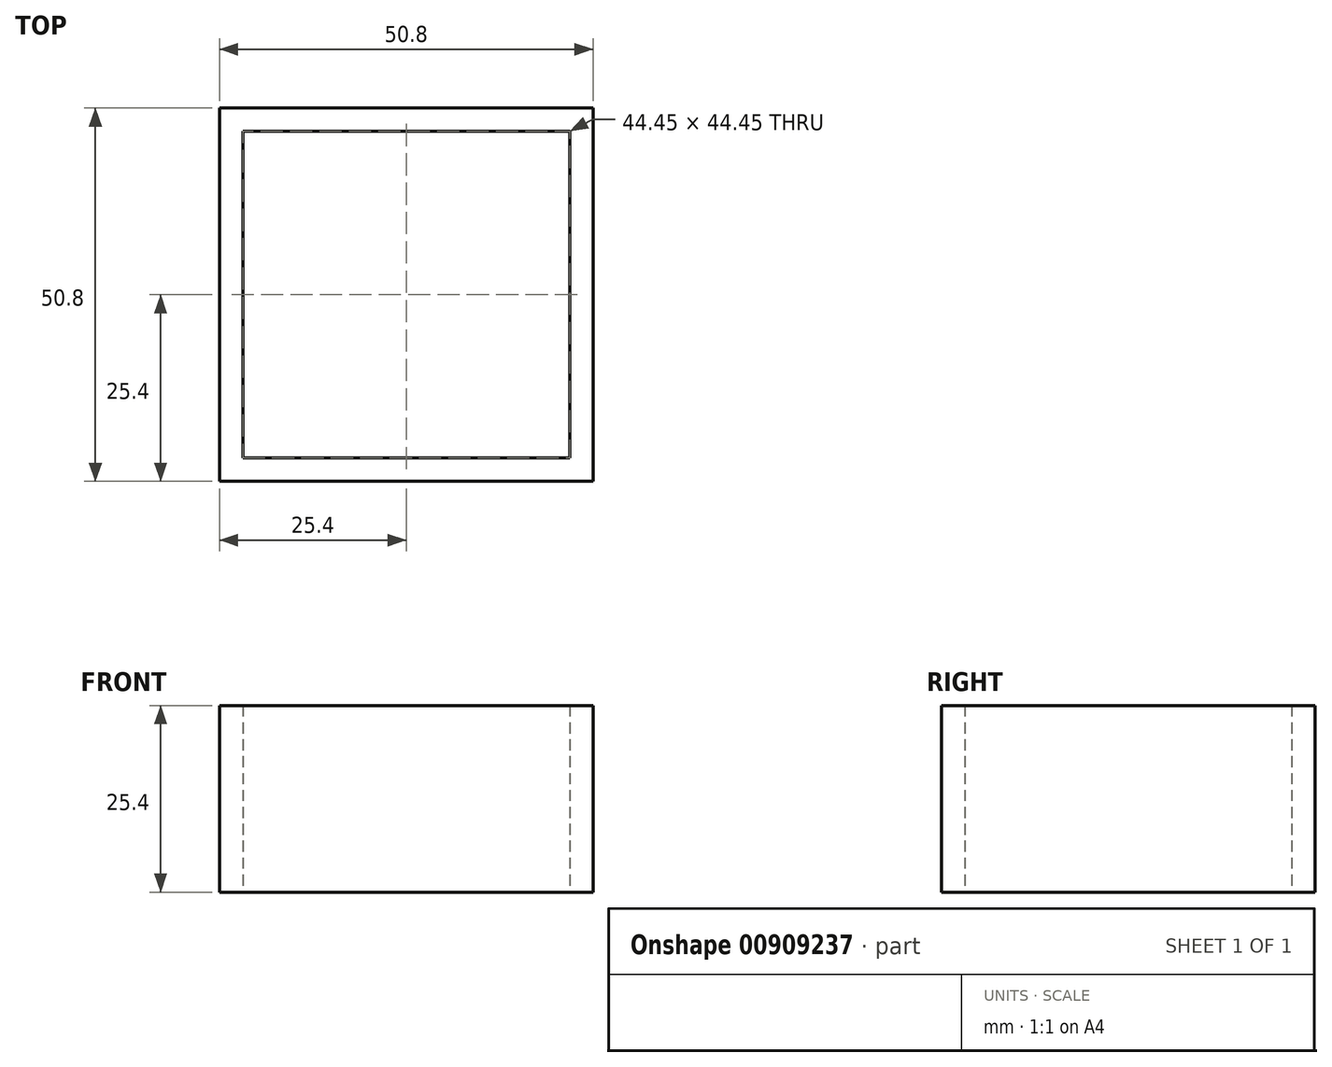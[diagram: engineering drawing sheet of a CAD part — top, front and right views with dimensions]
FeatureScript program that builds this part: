
annotation { "Feature Type Name" : "Feature", "Feature Type Description" : "" }
export const myFeature = defineFeature(function(context is Context, id is Id, definition is map)
    precondition{}
    {
        {
            var Q0;
            Q0=qCreatedBy(makeId("Top.planeOp"),FACE);
            var sketch = newSketch(context, id + "F0", { "sketchPlane" : qUnion([Q0])});
            skLineSegment(sketch, "E0.bottom", {"start": v(-25.4, -25.4) * mm, "end": v(25.4, -25.4) * mm});
            skLineSegment(sketch, "E0.top", {"start": v(-25.4, 25.4) * mm, "end": v(25.4, 25.4) * mm});
            skLineSegment(sketch, "E0.left", {"start": v(-25.4, -25.4) * mm, "end": v(-25.4, 25.4) * mm});
            skLineSegment(sketch, "E0.right", {"start": v(25.4, -25.4) * mm, "end": v(25.4, 25.4) * mm});
            skPoint(sketch, "E0.middle", {"position": v(0, 0) * mm});
            skLineSegment(sketch, "E1.bottom", {"start": v(-22.22, -22.22) * mm, "end": v(22.23, -22.22) * mm});
            skLineSegment(sketch, "E1.top", {"start": v(-22.23, 22.22) * mm, "end": v(22.22, 22.22) * mm});
            skLineSegment(sketch, "E1.left", {"start": v(-22.22, -22.22) * mm, "end": v(-22.23, 22.22) * mm});
            skLineSegment(sketch, "E1.right", {"start": v(22.23, -22.22) * mm, "end": v(22.22, 22.23) * mm});
            skSolve(sketch);
        }
        {
            var Q0;
            Q0=makeQuery(id+"F0.imprint","IMPRINT",FACE,{"disambiguationData":[TD([[makeQuery(id+"F0.imprint","IMPRINT",EDGE,{"derivedFrom":sQuery(id+"F0.wireOp",EDGE,"E0.bottom")}),1.0]])]});
            extrude(context, id + "F1", {"entities" : qUnion([Q0]), "depth" : 25.4 * mm, "offsetDistance" : 25.4 * mm});
        }
    });
